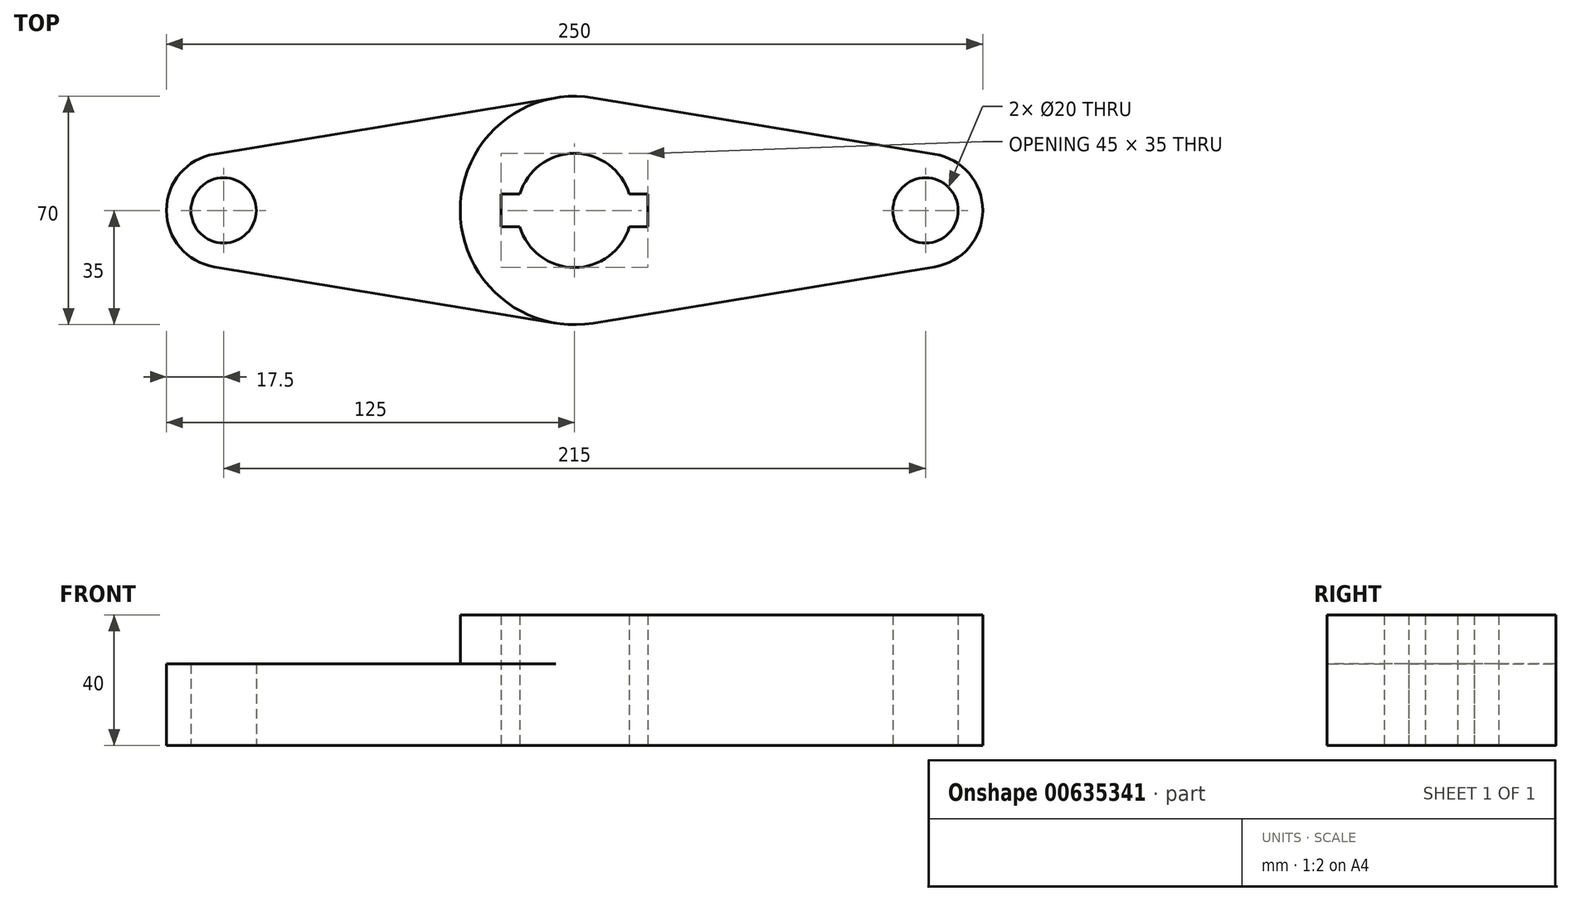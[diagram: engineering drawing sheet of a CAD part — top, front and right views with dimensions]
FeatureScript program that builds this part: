
annotation { "Feature Type Name" : "Feature", "Feature Type Description" : "" }
export const myFeature = defineFeature(function(context is Context, id is Id, definition is map)
    precondition{}
    {
        {
            var Q0;
            Q0=qCreatedBy(makeId("Top.planeOp"),FACE);
            var sketch = newSketch(context, id + "F0", { "sketchPlane" : qUnion([Q0])});
            skCircle(sketch, "E0", {"center": v(0, 0) * mm, "radius": 35 * mm});
            skCircle(sketch, "E1", {"center": v(107.5, 0) * mm, "radius": 17.5 * mm});
            skCircle(sketch, "E2", {"center": v(-107.5, 0) * mm, "radius": 17.5 * mm});
            skLineSegment(sketch, "E3", {"start": v(0, 0) * mm, "end": v(0, 79.73) * mm, "construction": true});
            skLineSegment(sketch, "E4", {"start": v(-110.35, 17.27) * mm, "end": v(-5.7, 34.53) * mm});
            skLineSegment(sketch, "E5", {"start": v(5.7, 34.53) * mm, "end": v(110.35, 17.27) * mm});
            skLineSegment(sketch, "E6", {"start": v(-5.7, -34.53) * mm, "end": v(-110.35, -17.27) * mm});
            skLineSegment(sketch, "E7", {"start": v(5.7, -34.53) * mm, "end": v(110.35, -17.27) * mm});
            skCircle(sketch, "E8", {"center": v(0, 0) * mm, "radius": 17.5 * mm});
            skCircle(sketch, "E9", {"center": v(-107.5, 0) * mm, "radius": 10 * mm});
            skCircle(sketch, "E10", {"center": v(107.5, 0) * mm, "radius": 10 * mm});
            skLineSegment(sketch, "E11.bottom", {"start": v(-22.5, 5) * mm, "end": v(22.5, 5) * mm});
            skLineSegment(sketch, "E11.top", {"start": v(-22.5, -5) * mm, "end": v(22.5, -5) * mm});
            skLineSegment(sketch, "E11.left", {"start": v(-22.5, 5) * mm, "end": v(-22.5, -5) * mm});
            skLineSegment(sketch, "E11.right", {"start": v(22.5, 5) * mm, "end": v(22.5, -5) * mm});
            skSolve(sketch);
        }
        {
            var Q0;
            {var subQ0=sQuery(id+"F0.wireOp",EDGE,"E5");Q0=makeQuery(id+"F0.imprint","IMPRINT",FACE,{"disambiguationData":[TD([[makeQuery(id+"F0.imprint","IMPRINT",EDGE,{"derivedFrom":subQ0}),-1.0]])]});}
            var Q1;
            {var subQ0=sQuery(id+"F0.wireOp",EDGE,"E11.left");Q1=makeQuery(id+"F0.imprint","IMPRINT",FACE,{"disambiguationData":[TD([[makeQuery(id+"F0.imprint","IMPRINT",EDGE,{"derivedFrom":subQ0}),-1.0]])]});}
            var Q2;
            Q2=makeQuery(id+"F0.imprint","IMPRINT",FACE,{"disambiguationData":[TD([[makeQuery(id+"F0.imprint","IMPRINT",EDGE,{"derivedFrom":sQuery(id+"F0.wireOp",EDGE,"E10")}),-1.0]])]});
            extrude(context, id + "F1", {"entities" : qUnion([Q0, Q1, Q2]), "depth" : 40 * mm});
        }
        {
            var Q0;
            {var subQ0=sQuery(id+"F0.wireOp",EDGE,"E4");Q0=makeQuery(id+"F0.imprint","IMPRINT",FACE,{"disambiguationData":[TD([[makeQuery(id+"F0.imprint","IMPRINT",EDGE,{"derivedFrom":subQ0}),-1.0]])]});}
            var Q1;
            Q1=makeQuery(id+"F0.imprint","IMPRINT",FACE,{"disambiguationData":[TD([[makeQuery(id+"F0.imprint","IMPRINT",EDGE,{"derivedFrom":sQuery(id+"F0.wireOp",EDGE,"E9")}),-1.0]])]});
            extrude(context, id + "F2", {"entities" : qUnion([Q0, Q1]), "operationType" : NewBodyOperationType.ADD, "depth" : 25 * mm});
        }
    });
